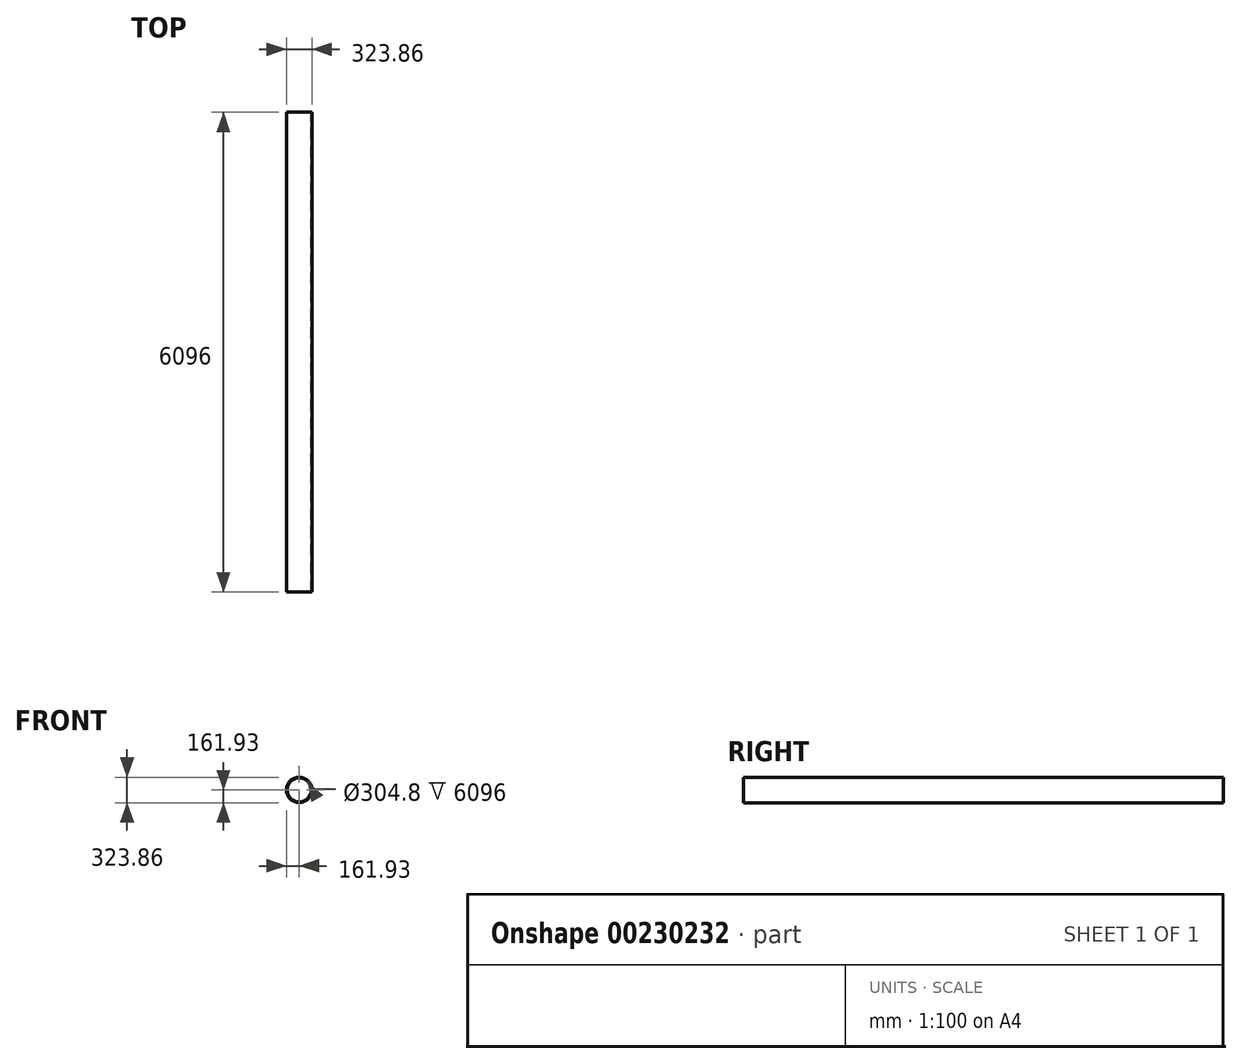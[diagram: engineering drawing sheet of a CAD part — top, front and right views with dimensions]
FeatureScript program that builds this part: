
annotation { "Feature Type Name" : "Feature", "Feature Type Description" : "" }
export const myFeature = defineFeature(function(context is Context, id is Id, definition is map)
    precondition{}
    {
        {
            var Q0;
            Q0=qCreatedBy(makeId("Front.planeOp"),FACE);
            var sketch = newSketch(context, id + "F0", { "sketchPlane" : qUnion([Q0])});
            skCircle(sketch, "E0", {"center": v(0, 0) * mm, "radius": 161.93 * mm});
            skCircle(sketch, "E1", {"center": v(0, 0) * mm, "radius": 152.4 * mm});
            skSolve(sketch);
        }
        {
            var Q0;
            Q0=qSketchRegion(id+"F0",true);
            extrude(context, id + "F1", {"entities" : qUnion([Q0]), "depth" : 6096 * mm});
        }
    });
